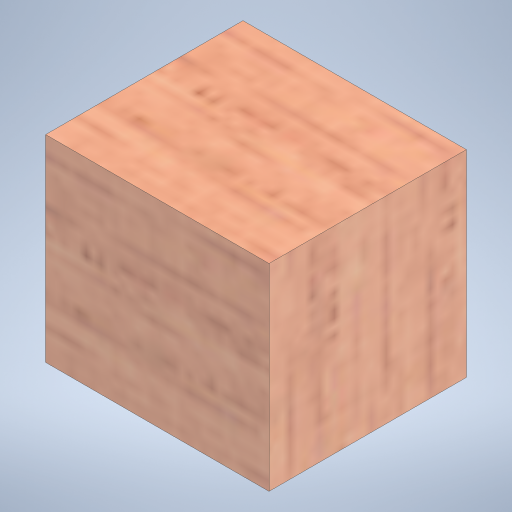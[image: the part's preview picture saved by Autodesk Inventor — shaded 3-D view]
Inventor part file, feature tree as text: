
AUTODESK INVENTOR PART (.ipt)
format: ipt  version: 2023 (Build 270158000, 158)  size: 330,240 bytes
history: native  units: mm
features: extrude x1, sketch x1
ambient origin geometry x8: Origin, YZ Plane, XZ Plane, XY Plane, X Axis, Y Axis, Z Axis, Center Point
bodies: Volumenkörper1 (feature_tree)
feature tree (2):
  extrude  "Extrusion1"  Depth=26.5mm
  sketch  "Skizze1"  dims[d0=26.5mm d1=26.5mm d2=30.0mm d3=0.0mm]
